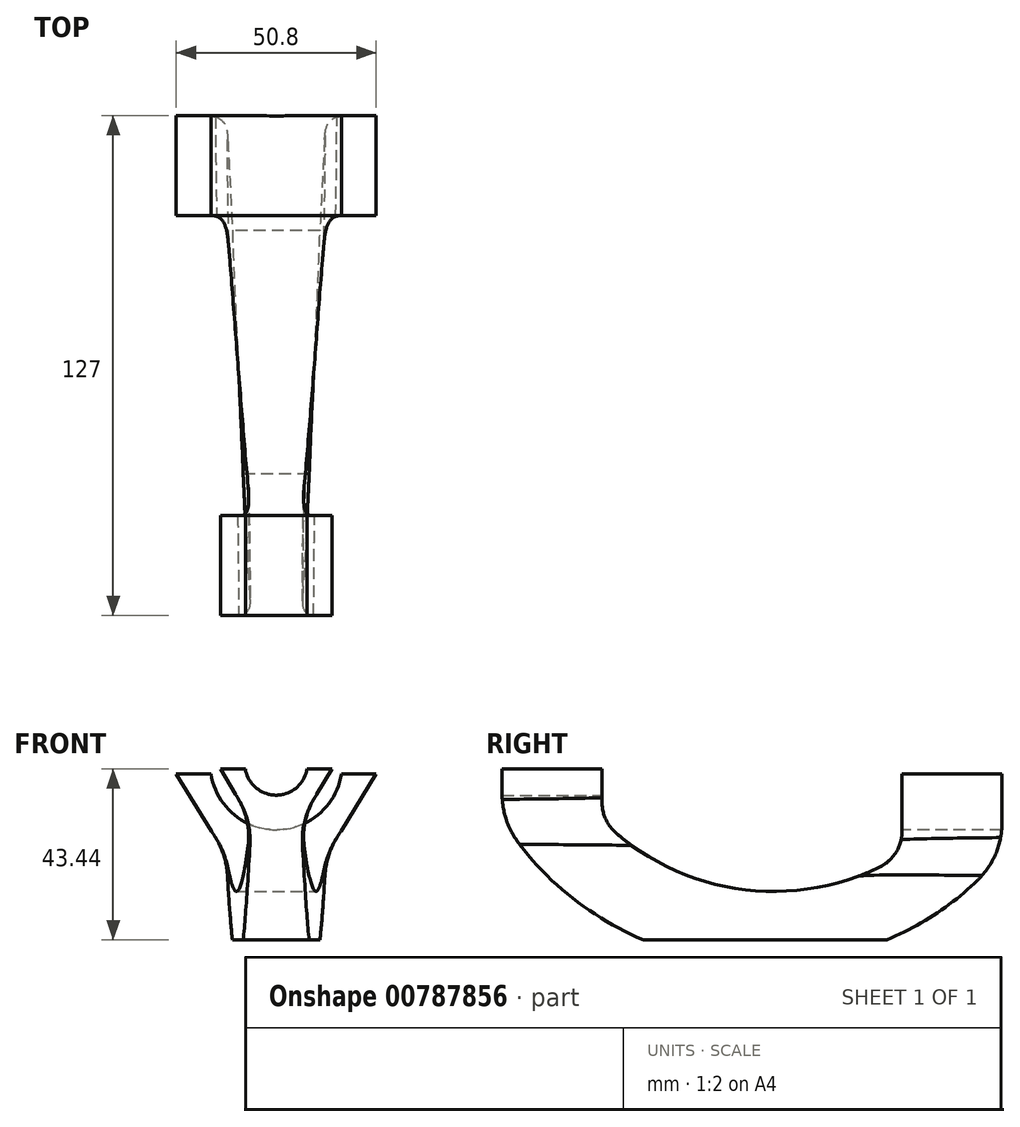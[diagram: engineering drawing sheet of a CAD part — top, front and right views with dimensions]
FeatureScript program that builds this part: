
annotation { "Feature Type Name" : "Feature", "Feature Type Description" : "" }
export const myFeature = defineFeature(function(context is Context, id is Id, definition is map)
    precondition{}
    {
        {
            var Q0;
            Q0=qCreatedBy(makeId("Front.planeOp"),FACE);
            var sketch = newSketch(context, id + "F0", { "sketchPlane" : qUnion([Q0])});
            skArc(sketch, "E0", {"start": v(-16.57, -2.54) * mm, "mid": v(0, -16.76) * mm, "end": v(16.57, -2.54) * mm});
            skLineSegment(sketch, "E1", {"start": v(16.57, -2.54) * mm, "end": v(25.4, -2.54) * mm});
            skLineSegment(sketch, "E2", {"start": v(25.4, -2.54) * mm, "end": v(12.7, -23.11) * mm});
            skLineSegment(sketch, "E3", {"start": v(12.7, -23.11) * mm, "end": v(-12.7, -23.11) * mm});
            skLineSegment(sketch, "E4", {"start": v(-12.7, -23.11) * mm, "end": v(-25.4, -2.54) * mm});
            skLineSegment(sketch, "E5", {"start": v(-25.4, -2.54) * mm, "end": v(-16.57, -2.54) * mm});
            skSolve(sketch);
        }
        {
            var Q0;
            Q0=qCreatedBy(makeId("Front.planeOp"),FACE);
            cPlane(context, id + "F1", {"entities" : qUnion([Q0]), "cplaneType" : CPlaneType.OFFSET, "offset" : 76.2 * mm, "width" : 152.4 * mm, "height" : 152.4 * mm});
        }
        {
            var Q0;
            Q0=qCreatedBy(id+"F1.planeOp",FACE);
            var sketch = newSketch(context, id + "F2", { "sketchPlane" : qUnion([Q0])});
            skArc(sketch, "E6", {"start": v(-7.84, -1.27) * mm, "mid": v(0, -7.94) * mm, "end": v(7.84, -1.27) * mm});
            skLineSegment(sketch, "E7", {"start": v(-7.84, -1.27) * mm, "end": v(-14.19, -1.27) * mm});
            skLineSegment(sketch, "E8", {"start": v(-14.19, -1.27) * mm, "end": v(-6.35, -14.29) * mm});
            skLineSegment(sketch, "E9", {"start": v(-6.35, -14.29) * mm, "end": v(6.35, -14.29) * mm});
            skLineSegment(sketch, "E10", {"start": v(6.35, -14.29) * mm, "end": v(14.19, -1.27) * mm});
            skLineSegment(sketch, "E11", {"start": v(14.19, -1.27) * mm, "end": v(7.84, -1.27) * mm});
            skSolve(sketch);
        }
        {
            var Q0;
            Q0 = qSketchRegion(id + "F0", true);
            extrude(context, id + "F3", {"entities" : qUnion([Q0]), "oppositeDirection" : true, "depth" : 25.4 * mm, "offsetDistance" : 25.4 * mm});
        }
        {
            var Q0;
            Q0 = qSketchRegion(id + "F2", true);
            extrude(context, id + "F4", {"entities" : qUnion([Q0]), "depth" : 25.4 * mm, "offsetDistance" : 25.4 * mm});
        }
        {
            var Q0;
            Q0=qCreatedBy(makeId("Right.planeOp"),FACE);
            var sketch = newSketch(context, id + "F5", { "sketchPlane" : qUnion([Q0])});
            skArc(sketch, "E12", {"start": v(-88.9, -14.29) * mm, "mid": v(-40.07, -41.39) * mm, "end": v(12.7, -23.11) * mm});
            skSolve(sketch);
        }
        {
            var Q0;
            Q0=sQuery(id+"F5.wireOp",EDGE,"E12");
            var Q1;
            Q1=makeQuery(id+"F3.opExtrude","SWEPT_FACE",FACE,{"disambiguationData":[OSD([sQuery(id+"F0.wireOp",EDGE,"E3")])]});
            var Q2;
            Q2=makeQuery(id+"F4.opExtrude","SWEPT_FACE",FACE,{"disambiguationData":[OSD([sQuery(id+"F2.wireOp",EDGE,"E9")])]});
            loft(context, id + "F6", {"addSections" : true, "spine" : qUnion([Q0]), "sectionCount" : 10, "sheetProfilesArray" : [{ "sheetProfileEntities" : qUnion([Q1]) }, { "sheetProfileEntities" : qUnion([Q2]) }]});
        }
        {
            var Q0;
            Q0=makeQuery(id+"F3.opExtrude","SWEPT_BODY",BODY,{"disambiguationData":[OSD([sQuery(id+"F0.wireOp",EDGE,"E0"),sQuery(id+"F0.wireOp",EDGE,"E1"),sQuery(id+"F0.wireOp",EDGE,"E2"),sQuery(id+"F0.wireOp",EDGE,"E3"),sQuery(id+"F0.wireOp",EDGE,"E4"),sQuery(id+"F0.wireOp",EDGE,"E5")])]});
            var Q1;
            Q1=makeQuery(id+"F4.opExtrude","SWEPT_BODY",BODY,{"disambiguationData":[OSD([sQuery(id+"F2.wireOp",EDGE,"E6"),sQuery(id+"F2.wireOp",EDGE,"E7"),sQuery(id+"F2.wireOp",EDGE,"E8"),sQuery(id+"F2.wireOp",EDGE,"E9"),sQuery(id+"F2.wireOp",EDGE,"E10"),sQuery(id+"F2.wireOp",EDGE,"E11")])]});
            var Q2;
            Q2=makeQuery(id+"F6.opLoft","SWEPT_BODY",BODY,{"disambiguationData":[OSD([sQuery(id+"F0.wireOp",EDGE,"E3"),sQuery(id+"F2.wireOp",EDGE,"E9")])]});
            booleanBodies(context, id + "F7", {"operationType" : BooleanOperationType.UNION, "tools" : qUnion([Q0, Q1, Q2])});
        }
        {
            var Q0;
            {var subQ0=sQuery(id+"F0.wireOp",EDGE,"E3");var subQ1=makeQuery(id+"F3.opExtrude","CAP_EDGE",EDGE,{"disambiguationData":[OSD([subQ0])],"isStart":true});var subQ2=sQuery(id+"F0.wireOp",EDGE,"E4");var subQ3=sQuery(id+"F0.wireOp",EDGE,"E2");Q0=makeQuery(id+"F7.opBoolean","MERGE",EDGE,{"derivedFrom":[subQ1,makeQuery(id+"F6.opLoft","MID_CAP_EDGE",EDGE,{"disambiguationData":[OSD([subQ3,subQ0,subQ2]),TDD([makeQuery(id+"F3.opExtrude","CAP_VERTEX",VERTEX,{"disambiguationData":[OSD([subQ3,subQ0])],"isStart":true}),makeQuery(id+"F3.opExtrude","CAP_VERTEX",VERTEX,{"disambiguationData":[OSD([subQ0,subQ2])],"isStart":true}),subQ1])],"capPos":0.0})]});}
            var Q1;
            {var subQ0=sQuery(id+"F2.wireOp",EDGE,"E9");var subQ1=makeQuery(id+"F4.opExtrude","CAP_EDGE",EDGE,{"disambiguationData":[OSD([subQ0])],"isStart":true});var subQ2=sQuery(id+"F2.wireOp",EDGE,"E10");var subQ3=sQuery(id+"F2.wireOp",EDGE,"E8");Q1=makeQuery(id+"F7.opBoolean","MERGE",EDGE,{"derivedFrom":[subQ1,makeQuery(id+"F6.opLoft","MID_CAP_EDGE",EDGE,{"disambiguationData":[OSD([subQ3,subQ0,subQ2]),TDD([makeQuery(id+"F4.opExtrude","CAP_VERTEX",VERTEX,{"disambiguationData":[OSD([subQ3,subQ0])],"isStart":true}),makeQuery(id+"F4.opExtrude","CAP_VERTEX",VERTEX,{"disambiguationData":[OSD([subQ0,subQ2])],"isStart":true}),subQ1])],"capPos":1.0})]});}
            fillet(context, id + "F8", {"entities" : qUnion([Q0, Q1]), "radius" : 10.16 * mm, "tangentPropagation" : true, "allowEdgeOverflow" : false});
        }
        {
            var Q0;
            {var subQ0=sQuery(id+"F0.wireOp",EDGE,"E4");var subQ1=sQuery(id+"F0.wireOp",EDGE,"E3");Q0=makeQuery(id+"F7.opBoolean","MERGE",EDGE,{"derivedFrom":[makeQuery(id+"F3.opExtrude","SWEPT_EDGE",EDGE,{"disambiguationData":[OSD([subQ1,subQ0])]}),makeQuery(id+"F6.opLoft","MID_CAP_EDGE",EDGE,{"disambiguationData":[OSD([subQ1,subQ0])],"capPos":0.0})]});}
            var Q1;
            {var subQ0=sQuery(id+"F0.wireOp",EDGE,"E3");var subQ1=sQuery(id+"F0.wireOp",EDGE,"E2");Q1=makeQuery(id+"F7.opBoolean","MERGE",EDGE,{"derivedFrom":[makeQuery(id+"F3.opExtrude","SWEPT_EDGE",EDGE,{"disambiguationData":[OSD([subQ1,subQ0])]}),makeQuery(id+"F6.opLoft","MID_CAP_EDGE",EDGE,{"disambiguationData":[OSD([subQ1,subQ0])],"capPos":0.0})]});}
            var Q2;
            {var subQ0=sQuery(id+"F0.wireOp",EDGE,"E3");var subQ1=makeQuery(id+"F3.opExtrude","CAP_EDGE",EDGE,{"disambiguationData":[OSD([subQ0])],"isStart":false});var subQ2=sQuery(id+"F0.wireOp",EDGE,"E4");var subQ3=sQuery(id+"F0.wireOp",EDGE,"E2");Q2=makeQuery(id+"F7.opBoolean","MERGE",EDGE,{"derivedFrom":[subQ1,makeQuery(id+"F6.opLoft","MID_CAP_EDGE",EDGE,{"disambiguationData":[OSD([subQ3,subQ0,subQ2]),TDD([makeQuery(id+"F3.opExtrude","CAP_VERTEX",VERTEX,{"disambiguationData":[OSD([subQ3,subQ0])],"isStart":false}),makeQuery(id+"F3.opExtrude","CAP_VERTEX",VERTEX,{"disambiguationData":[OSD([subQ0,subQ2])],"isStart":false}),subQ1])],"capPos":0.0})]});}
            var Q3;
            {var subQ0=sQuery(id+"F2.wireOp",EDGE,"E9");var subQ1=sQuery(id+"F2.wireOp",EDGE,"E8");Q3=makeQuery(id+"F7.opBoolean","MERGE",EDGE,{"derivedFrom":[makeQuery(id+"F4.opExtrude","SWEPT_EDGE",EDGE,{"disambiguationData":[OSD([subQ1,subQ0])]}),makeQuery(id+"F6.opLoft","MID_CAP_EDGE",EDGE,{"disambiguationData":[OSD([subQ1,subQ0])],"capPos":1.0})]});}
            var Q4;
            {var subQ0=sQuery(id+"F2.wireOp",EDGE,"E9");var subQ1=makeQuery(id+"F4.opExtrude","CAP_EDGE",EDGE,{"disambiguationData":[OSD([subQ0])],"isStart":false});var subQ2=sQuery(id+"F2.wireOp",EDGE,"E10");var subQ3=sQuery(id+"F2.wireOp",EDGE,"E8");Q4=makeQuery(id+"F7.opBoolean","MERGE",EDGE,{"derivedFrom":[subQ1,makeQuery(id+"F6.opLoft","MID_CAP_EDGE",EDGE,{"disambiguationData":[OSD([subQ3,subQ0,subQ2]),TDD([makeQuery(id+"F4.opExtrude","CAP_VERTEX",VERTEX,{"disambiguationData":[OSD([subQ3,subQ0])],"isStart":false}),makeQuery(id+"F4.opExtrude","CAP_VERTEX",VERTEX,{"disambiguationData":[OSD([subQ0,subQ2])],"isStart":false}),subQ1])],"capPos":1.0})]});}
            var Q5;
            {var subQ0=sQuery(id+"F2.wireOp",EDGE,"E10");var subQ1=sQuery(id+"F2.wireOp",EDGE,"E9");Q5=makeQuery(id+"F7.opBoolean","MERGE",EDGE,{"derivedFrom":[makeQuery(id+"F4.opExtrude","SWEPT_EDGE",EDGE,{"disambiguationData":[OSD([subQ1,subQ0])]}),makeQuery(id+"F6.opLoft","MID_CAP_EDGE",EDGE,{"disambiguationData":[OSD([subQ1,subQ0])],"capPos":1.0})]});}
            fillet(context, id + "F9", {"entities" : qUnion([Q0, Q1, Q2, Q3, Q4, Q5]), "radius" : 20.32 * mm, "tangentPropagation" : true, "allowEdgeOverflow" : false});
        }
        {
            var Q0;
            Q0=qCreatedBy(makeId("Front.planeOp"),FACE);
            var sketch = newSketch(context, id + "F10", { "sketchPlane" : qUnion([Q0])});
            skLineSegment(sketch, "E13.bottom", {"start": v(30.14, -57.98) * mm, "end": v(-44.9, -57.98) * mm});
            skLineSegment(sketch, "E13.top", {"start": v(30.14, -44.7) * mm, "end": v(-44.9, -44.7) * mm});
            skLineSegment(sketch, "E13.left", {"start": v(30.14, -57.98) * mm, "end": v(30.14, -44.7) * mm});
            skLineSegment(sketch, "E13.right", {"start": v(-44.9, -57.98) * mm, "end": v(-44.9, -44.7) * mm});
            skSolve(sketch);
        }
        {
            var Q0;
            Q0 = qSketchRegion(id + "F10", true);
            extrude(context, id + "F11", {"entities" : qUnion([Q0]), "operationType" : NewBodyOperationType.REMOVE, "depth" : 116.08 * mm, "offsetDistance" : 25.4 * mm});
        }
    });
